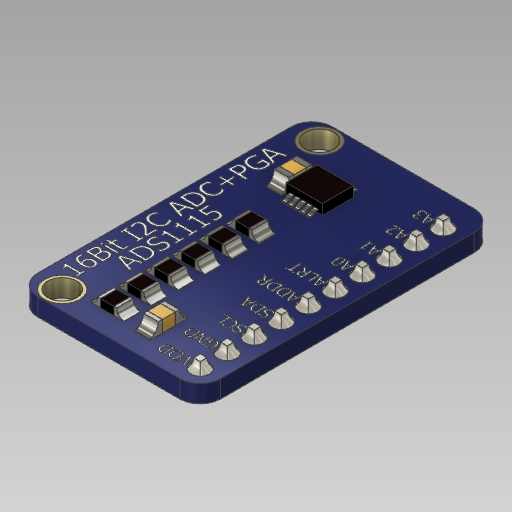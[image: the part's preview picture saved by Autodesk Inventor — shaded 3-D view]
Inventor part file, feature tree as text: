
AUTODESK INVENTOR PART (.ipt)
format: ipt  version: 2020 (Build 240168000, 168)  size: 1,989,120 bytes
history: native  units: in
note: dims shown in document units (in); Inventor stores cm internally (conversion verified against a paired STEP export)
features: sketch x18, extrude x15, projected_geometry x4, reference x4, other x4, mirror x3, fillet x2, plane x2, sweep x1, loft x1, pattern_linear x1
ambient origin geometry x8: Origin, YZ Plane, XZ Plane, XY Plane, X Axis, Y Axis, Z Axis, Center Point
bodies: Solid1 (feature_tree)
feature tree (55):
  extrude  "Extrusion1"  Depth=0.677in
  fillet  "Fillet1"  Radius=0.065in
  extrude  "Extrusion2"  Depth=0.107in
  extrude  "Extrusion3"  Depth=0.4765in
  mirror  "Mirror1"
  extrude  "Extrusion4"  TaperAngle=0.0deg  [1 undecoded]
  extrude  "Extrusion5"  Depth=0.0001in TaperAngle=0.0deg
  mirror  "Mirror2"
  extrude  "Extrusion6"  Depth=0.035in
  extrude  "Extrusion7"  Depth=3.937in
  extrude  "Extrusion8"  Depth=0.07in
  extrude  "Extrusion9"  Depth=0.0001in TaperAngle=0.0deg
  extrude  "Extrusion10"  Depth=0.06in
  extrude  "Extrusion11"  Depth=0.08in
  extrude  "Extrusion12"  Depth=0.03in TaperAngle=0.0deg
  extrude  "Extrusion13"  Depth=0.05in
  extrude  "Extrusion14"  Depth=0.01in
  sweep  "Sweep1"
  fillet  "Fillet2"  Radius=0.03in
  plane  "Work Plane1"
  mirror  "Mirror3"
  extrude  "Extrusion15"  Depth=0.115in
  plane  "Work Plane2"
  loft  "Loft1"
  pattern_linear  "Rectangular Pattern1"  Spacing1=0.038in  [1 undecoded]
  sketch  "Sketch1"  dims[d0=1.09in d1=0.677in d2=0.065in d3=0.0in]
  sketch  "Sketch2"  dims[d4=0.075in d5=0.107in]
  sketch  "Sketch3"  dims[d6=0.953in d7=0.4765in]
  sketch  "Sketch4"  dims[d8=0.0975in d9=0.0in d10=0.0in]
  sketch  "Sketch5"  dims[d11=0.13in d12=0.0001in d13=0.0in]
  projected_geometry  "Projected Loop1"
  sketch  "Sketch6"  dims[d14=0.035in d15=0.07in]
  sketch  "Sketch7"  dims[d16=0.07in d17=3.937in d19=0.1in d20=0.3937in d22=1.0in]
  sketch  "Sketch8"  dims[d24=0.0001in d25=0.0in d26=0.07in]
  sketch  "Sketch9"  dims[d27=3.937in d29=0.1in d30=0.3937in d32=1.0in d34=0.0001in d35=0.0in]
  sketch  "Sketch10"  dims[d36=0.125in d37=0.06in]
  sketch  "Sketch11"  dims[d38=0.19in d39=0.08in]
  sketch  "Sketch12"  dims[d40=2.3622in d42=0.1in d43=0.3937in d45=1.0in d47=0.03in d48=0.0in]
  projected_geometry  "Projected Loop2"
  sketch  "Sketch13"  dims[d52=0.001in d53=0.05in]
  projected_geometry  "Projected Loop3"
  sketch  "Sketch14"  dims[d54=0.0001in d55=0.01in]
  projected_geometry  "Projected Loop4"
  sketch  "Sketch15"  dims[d56=0.03in d57=0.0in d58=0.0001in]
  sketch  "Sketch16"  dims[d59=2.3622in d61=0.1in d62=0.3937in d64=1.0in d66=0.03in d67=0.0in]
  sketch  "Sketch17"  dims[d68=0.1875in d69=0.115in]
  sketch  "Sketch19"  dims[d70=0.135in d71=0.335in d72=0.038in d73=0.0in d74=0.14in d75=0.055in d76=0.068in d77=0.254in d78=0.148in d79=0.175in d80=0.044in d81=0.0in d82=0.002in d83=0.039in d84=0.048in d85=0.0005in d86=0.044in d87=0.0in d88=0.0001in d89=0.0001in d90=0.044in d91=0.0in d92=0.002in d93=0.0005in d94=0.042in d95=0.045in d96=0.044in d97=0.0in d98=0.0001in d99=0.0001in d100=0.044in d101=0.0in d102=0.015in d103=0.003in d104=0.135in d105=0.015in d106=0.025in d107=1.9685in d109=0.0225in d110=0.3937in d112=1.0in d114=0.015in d115=0.0265in d116=0.032in d117=0.0015in d118=0.0in d119=0.0in d120=0.002in d121=0.04in d122=0.125in d123=0.05in d124=0.0001in d125=0.0in d126=0.06in d127=0.107in d128=0.75in d129=0.065in d130=0.02in d131=0.125in d132=0.01in d133=0.375in d134=0.035in d135=0.0in d136=90.0deg d139=0.3937in d140=90.0deg d141=3.937in d143=0.1in]
  reference  "Reference1"
  reference  "Reference2"
  reference  "Reference3"
  reference  "Reference4"
  other  "Edges1"
  parser-record x1  (decoder bookkeeping rows leaked as tree rows — omitted from the tree; the rows remain in map.json)
  other  "Data Acquisition_R2.iam"
  other  "10 pin header:1"
note: 2 required parameter values undecoded (feature->parameter linkage not recoverable at this tier; creation-order binding heuristic only, values carry confidence <= 0.55)
note: 1 file-system path scrubbed to <path> (originals preserved in map.json)
